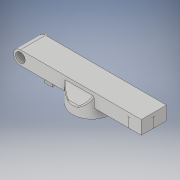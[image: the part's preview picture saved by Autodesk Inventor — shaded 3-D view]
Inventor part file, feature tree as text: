
AUTODESK INVENTOR PART (.ipt)
format: ipt  version: 2019 (Build 230136000, 136)  size: 247,296 bytes
history: native  units: in
note: dims shown in document units (in); Inventor stores cm internally (conversion verified against a paired STEP export)
features: sketch x9, extrude x5, chamfer x2, fillet x2
ambient origin geometry x8: Origin, YZ Plane, XZ Plane, XY Plane, X Axis, Y Axis, Z Axis, Center Point
bodies: Solid1 (feature_tree)
feature tree (18):
  extrude  "Extrusion1"  Depth=2.4606in
  extrude  "Extrusion2"  Depth=0.5118in TaperAngle=0.0deg
  extrude  "Extrusion3"  Depth=0.1969in TaperAngle=0.0deg
  sketch  "Sketch4"  dims[d9=2.2047in]
  chamfer  "Chamfer1"  Distance=0.1969in
  chamfer  "Chamfer2"  Distance=0.1181in Angle=120.0deg
  extrude  "Extrusion4"  Depth=0.2362in TaperAngle=0.0deg
  fillet  "Fillet2"  Radius=0.0394in
  fillet  "Fillet3"  Radius=0.0394in
  sketch  "Sketch6"  dims[d15=0.2559in]
  sketch  "Sketch7"  dims[d16=0.2559in d17=0.1181in d18=0.0787in d19=120.0deg]
  sketch  "Sketch8"  dims[d20=0.1181in d21=0.0787in d22=120.0deg d25=0.2362in d26=0.0in d28=0.0394in d29=0.0394in]
  sketch  "Sketch9"  dims[d30=1.3386in d32=0.1575in d33=0.1575in d34=0.315in d35=0.1772in d36=0.0394in d37=0.0787in d39=0.1496in d41=0.1102in d42=0.1575in d43=0.0in]
  extrude  "Extrusion5"  Depth=0.1575in
  sketch  "Sketch1"  dims[d0=0.1969in d2=2.4606in]
  sketch  "Sketch2"  dims[d3=0.1378in d4=0.5118in d5=0.0in]
  sketch  "Sketch3"  dims[d6=0.5118in d7=0.1969in d8=0.0in]
  sketch  "Sketch5"  dims[d11=0.7874in d13=0.1969in d14=0.0in]
